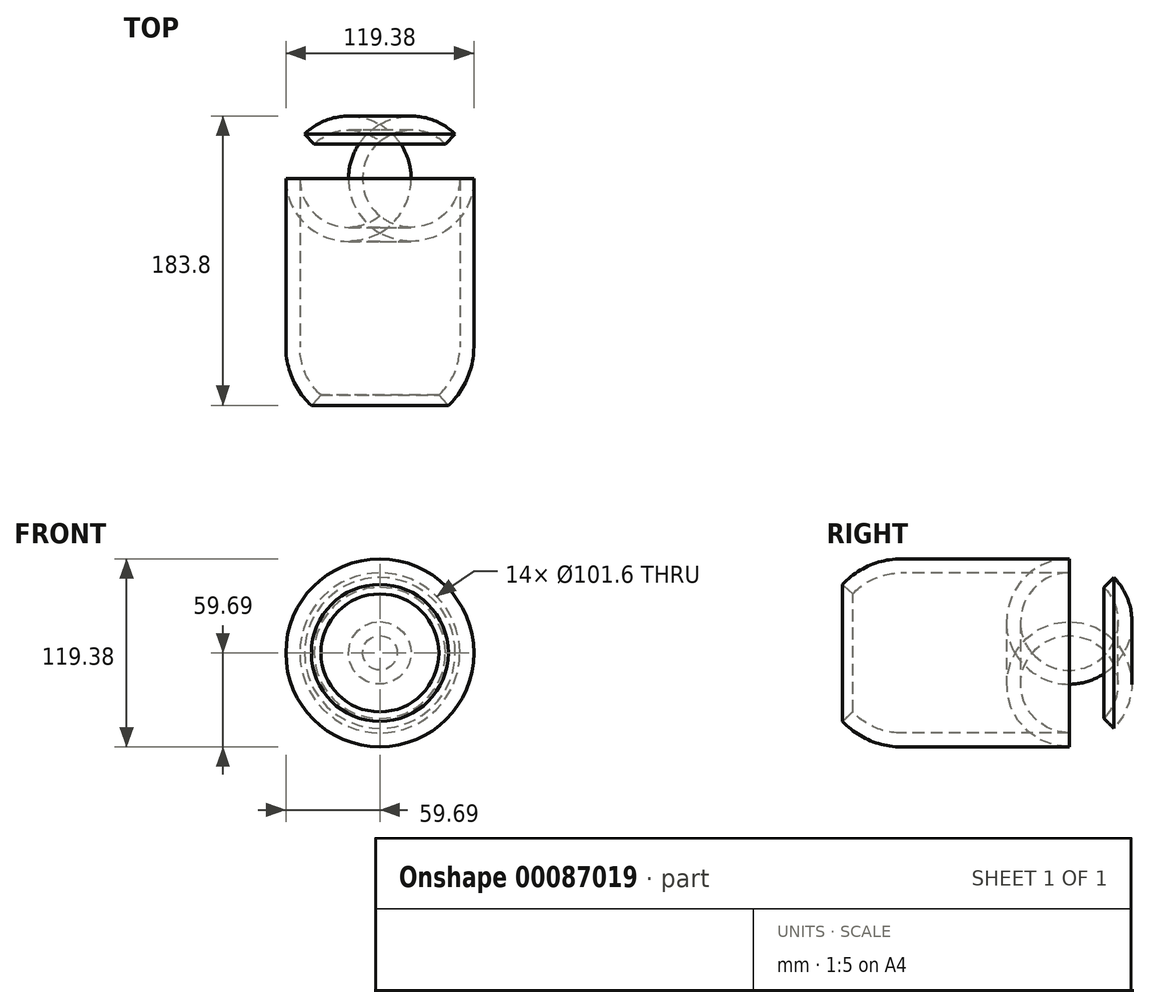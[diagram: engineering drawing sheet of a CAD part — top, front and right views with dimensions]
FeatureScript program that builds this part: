
annotation { "Feature Type Name" : "Feature", "Feature Type Description" : "" }
export const myFeature = defineFeature(function(context is Context, id is Id, definition is map)
    precondition{}
    {
        {
            var Q0;
            Q0=qCreatedBy(makeId("Right.planeOp"),FACE);
            var sketch = newSketch(context, id + "F0", { "sketchPlane" : qUnion([Q0])});
            skLineSegment(sketch, "E0", {"start": v(-54.55, 50.8) * mm, "end": v(52.32, 50.8) * mm});
            skArc(sketch, "E1", {"start": v(-54.55, 50.8) * mm, "mid": v(-71.25, 47.32) * mm, "end": v(-85.16, 37.44) * mm});
            skArc(sketch, "E2", {"start": v(74.3, 41.62) * mm, "mid": v(64.23, 48.41) * mm, "end": v(52.32, 50.8) * mm});
            skArc(sketch, "E3.0", {"start": v(-54.55, 59.7) * mm, "mid": v(-74.8, 55.46) * mm, "end": v(-91.68, 43.49) * mm});
            skLineSegment(sketch, "E3.1", {"start": v(-54.55, 59.7) * mm, "end": v(52.32, 59.7) * mm});
            skArc(sketch, "E3.2", {"start": v(80.63, 47.86) * mm, "mid": v(67.66, 56.61) * mm, "end": v(52.32, 59.7) * mm});
            skLineSegment(sketch, "E4", {"start": v(-91.68, 43.49) * mm, "end": v(-85.16, 37.44) * mm});
            skLineSegment(sketch, "E5", {"start": v(80.63, 47.86) * mm, "end": v(74.3, 41.62) * mm});
            skLineSegment(sketch, "E6", {"start": v(-75.7, 0) * mm, "end": v(76.53, 0) * mm});
            skSolve(sketch);
        }
        {
            var Q0;
            Q0=makeQuery(id+"F0.imprint","IMPRINT",FACE,{"disambiguationData":[TD([[makeQuery(id+"F0.imprint","IMPRINT",EDGE,{"derivedFrom":sQuery(id+"F0.wireOp",EDGE,"E0")}),1.0]])]});
            var Q1;
            Q1=sQuery(id+"F0.wireOp",EDGE,"E6");
            revolve(context, id + "F1", {"entities" : qUnion([Q0]), "axis" : qUnion([Q1]), "revolveType" : RevolveType.FULL});
        }
        {
            var Q0;
            Q0=qCreatedBy(makeId("Right.planeOp"),FACE);
            var sketch = newSketch(context, id + "F2", { "sketchPlane" : qUnion([Q0])});
            skCircle(sketch, "E7", {"center": v(-19.05, 0) * mm, "radius": 5.42 * mm});
            skCircle(sketch, "E8", {"center": v(39.75, 0) * mm, "radius": 7 * mm});
            skSolve(sketch);
        }
        {
            var Q0;
            Q0=sQuery(id+"F2.wireOp",EDGE,"E7");
            extrude(context, id + "F3", {"bodyType" : ToolBodyType.SURFACE, "surfaceEntities" : qUnion([Q0]), "endBound" : BoundingType.SYMMETRIC, "depth" : 222.17 * mm});
        }
    });
